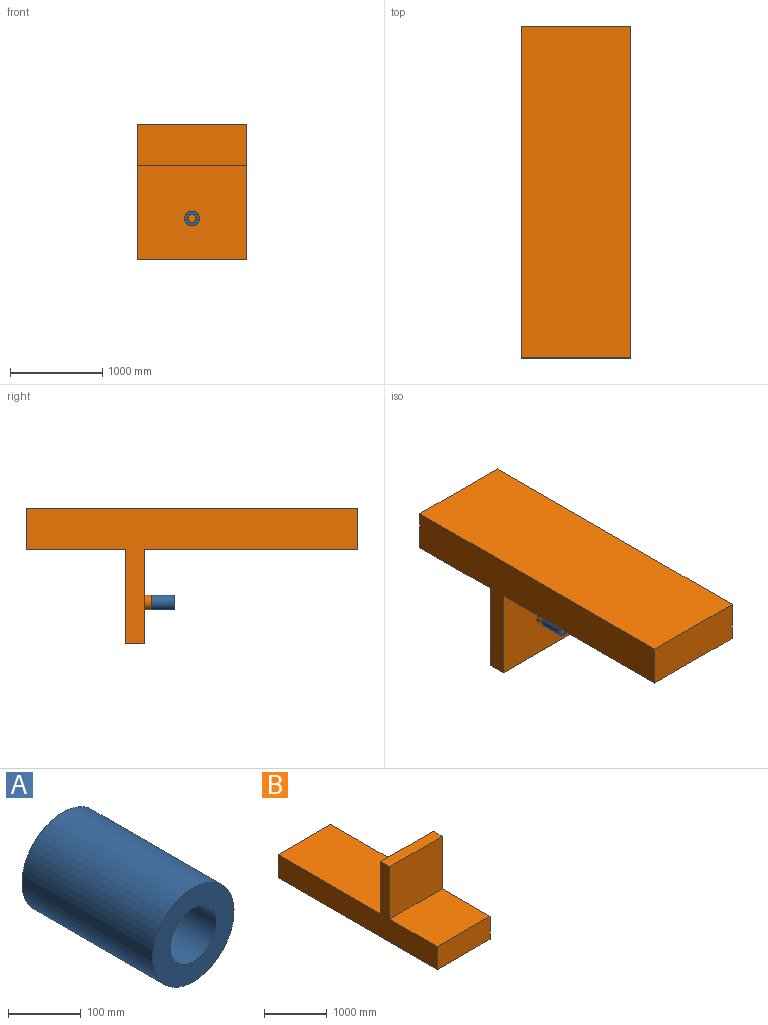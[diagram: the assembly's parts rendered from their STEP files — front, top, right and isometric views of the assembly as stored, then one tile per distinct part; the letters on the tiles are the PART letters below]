
ASSEMBLY  parts=2 mates=1
PART A: 4 faces, bbox 158.5x254x158.5 mm
  f0: cylinder r=45mm len=254mm, axis (0,-1,0), area 71816.8mm2, adj f2,f3
  f1: cylinder r=79.25mm len=254mm, axis (0,-1,0), area 126477.4mm2, adj f2,f3
  f2: plane 158.5x158.5mm, normal (0,1,0), area 13369.2mm2, adj f0,f1
  f3: plane 158.5x158.5mm, normal (0,-1,0), area 13369.2mm2, adj f0,f1
PART B: 12 faces, bbox 1190x3600x1475 mm
  f0: plane 3600x1190mm, normal (0,0,-1), area 4284000mm2, adj f1,f7,f8,f9
  f1: plane 1190x450mm, normal (0,1,0), area 535500mm2, adj f0,f2,f8,f9
  f2: plane 2320x1190mm, normal (0,0,1), area 2760800mm2, adj f1,f3,f8,f9
  f3: plane 1190x1025mm, normal (0,1,0), area 1200019mm2, adj f2,f4,f8,f9,f10
  f4: plane 1190x203.2mm, normal (0,0,1), area 241808mm2, adj f3,f5,f8,f9
  f5: plane 1190x1025mm, normal (0,-1,0), area 1219750mm2, adj f4,f6,f8,f9
  f6: plane 1190x1076.8mm, normal (0,0,1), area 1281392mm2, adj f5,f7,f8,f9
  f7: plane 1190x450mm, normal (0,-1,0), area 535500mm2, adj f0,f6,f8,f9
  f8: plane 3600x1475mm, normal (1,0,0), area 1828280mm2, adj f0,f1,f2,f3,f4,f5,f6,f7
  f9: plane 3600x1475mm, normal (-1,0,0), area 1828280mm2, adj f0,f1,f2,f3,f4,f5,f6,f7
  f10: cylinder r=79.25mm len=158.5mm, axis (0,-1,0), area 37843.6mm2, adj f3,f11
  f11: plane 158.5x158.5mm, normal (0,1,0), area 19731mm2, adj f10
PLACE A t=(-1985.2,814.03,329.98)mm
PLACE B rot(axis=(1,0,0),180deg) t=(-1985.2,730.1,329.98)mm
MATE cylindrical B.f10 <-> A.f1  axis (0,-1,0) through (-1985.2,895.53,329.98)mm
